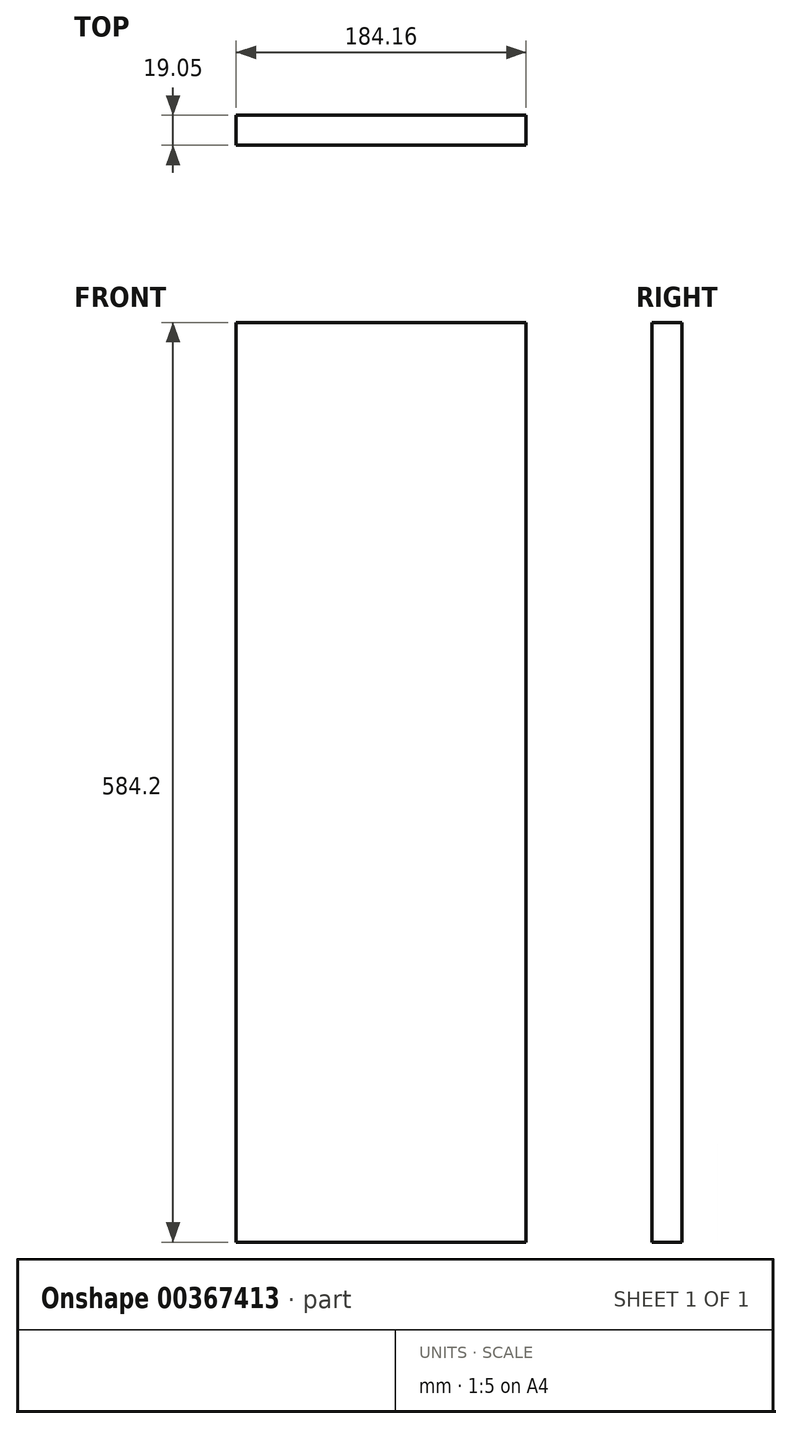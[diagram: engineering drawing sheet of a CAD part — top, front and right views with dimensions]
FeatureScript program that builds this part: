
annotation { "Feature Type Name" : "Feature", "Feature Type Description" : "" }
export const myFeature = defineFeature(function(context is Context, id is Id, definition is map)
    precondition{}
    {
        {
            var Q0;
            Q0=qCreatedBy(makeId("Front.planeOp"),FACE);
            var sketch = newSketch(context, id + "F0", { "sketchPlane" : qUnion([Q0])});
            skLineSegment(sketch, "E0.bottom", {"start": v(92.08, 292.1) * mm, "end": v(-92.07, 292.1) * mm});
            skLineSegment(sketch, "E0.top", {"start": v(92.07, -292.1) * mm, "end": v(-92.08, -292.1) * mm});
            skLineSegment(sketch, "E0.left", {"start": v(92.08, 292.1) * mm, "end": v(92.07, -292.1) * mm});
            skLineSegment(sketch, "E0.right", {"start": v(-92.07, 292.1) * mm, "end": v(-92.08, -292.1) * mm});
            skPoint(sketch, "E0.middle", {"position": v(0, 0) * mm});
            skSolve(sketch);
        }
        {
            var Q0;
            Q0 = qSketchRegion(id + "F0", true);
            extrude(context, id + "F1", {"entities" : qUnion([Q0]), "depth" : 19.05 * mm});
        }
    });
